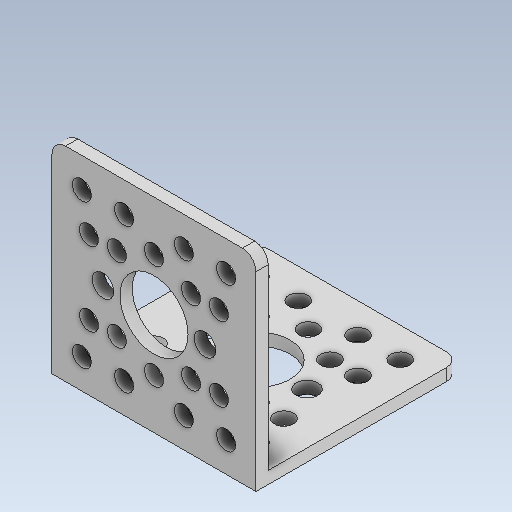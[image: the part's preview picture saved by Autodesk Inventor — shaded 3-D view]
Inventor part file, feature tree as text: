
AUTODESK INVENTOR PART (.ipt)
format: ipt  version: 2020 (Build 240168000, 168)  size: 195,584 bytes
history: native  units: in
note: dims shown in document units (in); Inventor stores cm internally (conversion verified against a paired STEP export)
features: fillet x1
ambient origin geometry x8: Origin, YZ Plane, XZ Plane, XY Plane, X Axis, Y Axis, Z Axis, Center Point
bodies: Solid1 (feature_tree)
feature tree (1):
  fillet  "Fillet1"  [1 undecoded]
note: 1 required parameter value undecoded (feature->parameter linkage not recoverable at this tier; creation-order binding heuristic only, values carry confidence <= 0.55)
